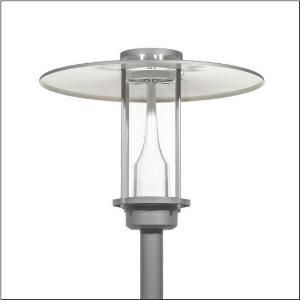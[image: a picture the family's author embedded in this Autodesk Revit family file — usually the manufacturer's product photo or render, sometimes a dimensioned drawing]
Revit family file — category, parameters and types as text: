
# Revit family: city-light_plus_iq___st1_2a_5xa5275ef14h000022_292e
name_source: partatom
category: Lighting Fixtures
units: mm (PartAtom-declared; Revit-internal decimal feet)

## family parameters
Cut with Voids When Loaded = No
Host = Face
Light Source = No
Part Type = Normal
Room Calculation Point = No
Round Connector Dimension = Use Diameter
Shared = No

## types (1)
- --- (1 x LED, 1470 lm, 10.5 W, 3000K)
    Apparent Load = 11 VA
    CIE Flux Codes = 22 62 93 97 100
    Color Rendering = 70
    Color Temperature = 3000K
    Default Elevation = 1800 mm
    Description = City-Light Plus iQ, mast luminaire, Module 540 iQ-SR, primary light control with 3 zone facetted reflector, of plastic, silver coated, highly specular, structured, primary optical cover: cover, of PMMA, transparent, light distribution: ST1.2a, light emission: direct distribution, primary light characteristic: asymmetric, installation type: post-top, LED, High Power LED, rated luminous flux: 1.470lm, luminous efficacy: 140lm/W, light colour: 730, colour temperature: 3000K, control gear: ECG iQ, control: Street-Remote, Auto-Match, Temp-Guard, Lumen-Switch, Night-Set, Smart-Wire, Light-Fading, Desk-Remote (wireless, voltage-free reading and setting of iQ features in the workshop via application-optimized NFC function/RFID function), optimised constant luminous flux control (CLO 2.0), pre-setting: logarithmic dimming characteristic, mains connection: 230..240V, AC, 50/60Hz, connection cable pre-assembled, cable length: 5,5m, wiring characteristics: H07RN-F, start of lifetime: 11W, end of service life: 11W, reduction: 5W, luminaire housing, upper part, of glass-fibre reinforced polyester, coated, Siteco® metallic grey (DB 702S), diameter: 750mm, height: 590mm, spigot size: d x l = 76 x 70mm (post-top) | with reducer (optional accessory) 60 x 70mm, post-top mast mounting element, of diecast aluminium, coated, Siteco® metallic grey (DB 702S), Module 540 iQ-SR, traffic white (RAL 9016), equipment: standard, protection rating (complete): IP65, insulation class (complete): insulation class II (safety insulation), certification: CE, ENEC, VDE, packaging unit: 1 piece

Light Distribution: ST1.2a
    Height = 590 mm
    Lamp = 1 x LED
    Lamp Light Flux = 1470 lm
    Lamp Power = 10.5 W
    Lamp count = 1
    Length = 750 mm
    Luminous efficacy = 140 lm/W
    Manufacturer = Siteco
    ModVariant = No
    Model = 5XA5275EF14H000022
    Number of Poles = 1
    OnlyDefault = Yes
    Power Factor = 1
    Product Name = City-Light Plus iQ | ST1.2a
    Product group = mast luminaire | pylon top
    ProductGroupID = 6100
    Protection Class = Protection class II
    Protection Degree = IP 65
    RLX_Detail_Level = 1
    RLX_Emergency_Light_Flux = 0 lm
    RLX_Emergency_Type = 0
    RLX_Emergency_Type_DB = No
    RlxData = <blob elided: 51757 chars, md5=61f61139>
    Socket = socket
    Standby Power = 0 W
    System Light Flux = 1470 lm
    System Power = 11 W
    Type Comments = factory setting: luminous flux: 100 % | dim-lin: 254 | 419 mA
    Type Image = l_1006456.jpg
    URL = http://relux.com
    VarID = @adj_130409
    Voltage = 0 V
    Weight = 0.00 kg
    Width = 0 mm  [stored 0 ft]

note: [stored X ft] marks values corroborated as IEEE doubles in the binary element streams (Revit-internal decimal feet)

## geometry (parser evidence)
native form markers: Blend x4, Sweep x10
no freeform markers — native parametric forms only
